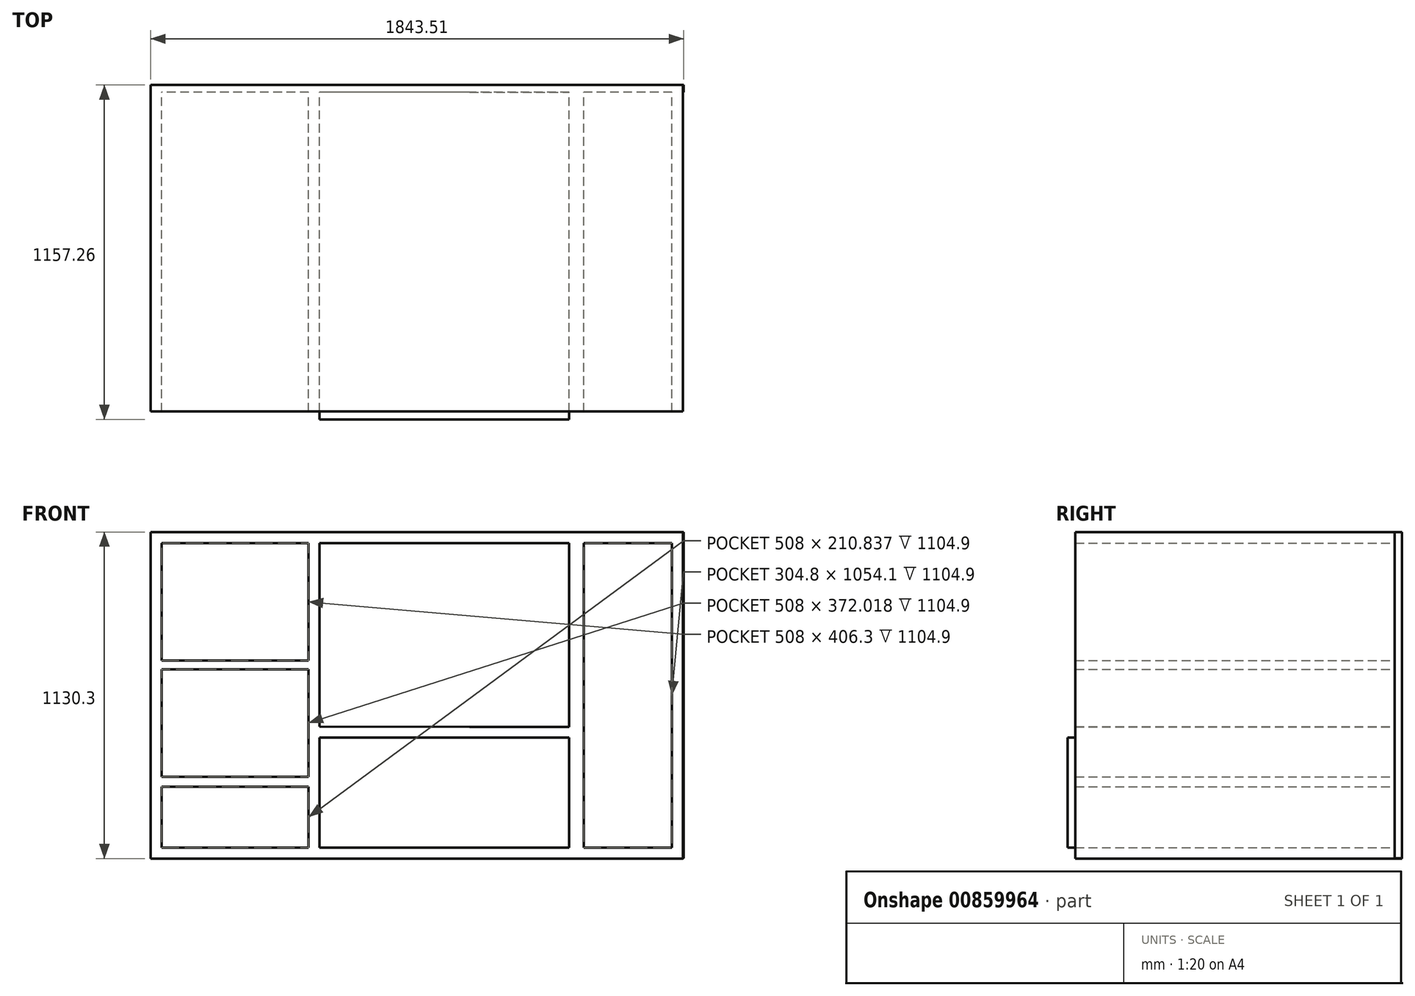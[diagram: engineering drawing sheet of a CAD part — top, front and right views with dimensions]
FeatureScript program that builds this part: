
annotation { "Feature Type Name" : "Feature", "Feature Type Description" : "" }
export const myFeature = defineFeature(function(context is Context, id is Id, definition is map)
    precondition{}
    {
        {
            var Q0;
            Q0=qCreatedBy(makeId("Front.planeOp"),FACE);
            var sketch = newSketch(context, id + "F0", { "sketchPlane" : qUnion([Q0])});
            skLineSegment(sketch, "E0.bottom", {"start": v(920.75, -565.15) * mm, "end": v(-920.75, -565.15) * mm});
            skLineSegment(sketch, "E0.top", {"start": v(920.75, 565.15) * mm, "end": v(-920.75, 565.15) * mm});
            skLineSegment(sketch, "E0.left", {"start": v(920.75, -565.15) * mm, "end": v(920.75, 565.15) * mm});
            skLineSegment(sketch, "E0.right", {"start": v(-920.75, -565.15) * mm, "end": v(-920.75, 565.15) * mm});
            skPoint(sketch, "E0.middle", {"position": v(0, 0) * mm});
            skLineSegment(sketch, "E1.bottom", {"start": v(882.65, -527.05) * mm, "end": v(-882.65, -527.05) * mm});
            skLineSegment(sketch, "E1.top", {"start": v(882.65, 527.05) * mm, "end": v(-882.65, 527.05) * mm});
            skLineSegment(sketch, "E1.left", {"start": v(882.65, -527.05) * mm, "end": v(882.65, 527.05) * mm});
            skLineSegment(sketch, "E2", {"start": v(-336.55, 0) * mm, "end": v(-336.55, -527.05) * mm});
            skLineSegment(sketch, "E3", {"start": v(-336.55, 0) * mm, "end": v(-336.55, 527.05) * mm});
            skPoint(sketch, "E4.start.orphan", {"position": v(-920.75, 0) * mm});
            skLineSegment(sketch, "E5", {"start": v(-882.65, 527.05) * mm, "end": v(-882.65, -527.05) * mm});
            skLineSegment(sketch, "E6", {"start": v(-374.65, -120.67) * mm, "end": v(-374.65, -527.05) * mm});
            skLineSegment(sketch, "E7", {"start": v(-374.65, -120.67) * mm, "end": v(-374.65, 527.05) * mm});
            skLineSegment(sketch, "E8", {"start": v(527.05, -148.89) * mm, "end": v(527.05, -527.05) * mm});
            skLineSegment(sketch, "E9", {"start": v(527.05, -527.05) * mm, "end": v(527.05, -148.89) * mm});
            skLineSegment(sketch, "E10", {"start": v(527.05, -148.89) * mm, "end": v(527.05, 527.05) * mm});
            skLineSegment(sketch, "E11", {"start": v(577.85, -145.72) * mm, "end": v(577.85, -527.05) * mm});
            skLineSegment(sketch, "E12", {"start": v(577.85, -145.72) * mm, "end": v(577.85, 527.05) * mm});
            skPoint(sketch, "E13.orphan", {"position": v(215.3, 0) * mm});
            skPoint(sketch, "E14.end.orphan", {"position": v(-280.78, 0) * mm});
            skLineSegment(sketch, "E15", {"start": v(-336.55, -146.05) * mm, "end": v(527.05, -148.89) * mm});
            skPoint(sketch, "E16.end.orphan", {"position": v(-180.7, -146.05) * mm});
            skLineSegment(sketch, "E17", {"start": v(182.89, -147.76) * mm, "end": v(182.89, -109.66) * mm});
            skLineSegment(sketch, "E18", {"start": v(182.89, -109.66) * mm, "end": v(-336.55, -107.95) * mm});
            skLineSegment(sketch, "E19", {"start": v(182.89, -109.66) * mm, "end": v(527.05, -109.66) * mm});
            skLineSegment(sketch, "E20", {"start": v(-882.65, -316.21) * mm, "end": v(-374.65, -316.21) * mm});
            skPoint(sketch, "E21.end.orphan", {"position": v(-374.65, 203.19) * mm});
            skLineSegment(sketch, "E22", {"start": v(-882.65, 120.75) * mm, "end": v(-374.65, 120.75) * mm});
            skLineSegment(sketch, "E23.bottom", {"start": v(-882.65, 120.75) * mm, "end": v(-752.77, 120.75) * mm});
            skLineSegment(sketch, "E23.top", {"start": v(-882.65, 120.75) * mm, "end": v(-752.77, 120.75) * mm});
            skLineSegment(sketch, "E23.left", {"start": v(-882.65, 120.75) * mm, "end": v(-882.65, 120.75) * mm});
            skLineSegment(sketch, "E23.right", {"start": v(-752.77, 120.75) * mm, "end": v(-752.77, 120.75) * mm});
            skLineSegment(sketch, "E24.bottom", {"start": v(-882.65, 89.88) * mm, "end": v(-408.51, 89.88) * mm});
            skLineSegment(sketch, "E24.top", {"start": v(-882.65, -282.14) * mm, "end": v(-408.51, -282.14) * mm});
            skLineSegment(sketch, "E24.left", {"start": v(-882.65, 89.88) * mm, "end": v(-882.65, -282.14) * mm});
            skLineSegment(sketch, "E25", {"start": v(-408.51, -282.14) * mm, "end": v(-374.65, -282.14) * mm});
            skLineSegment(sketch, "E26", {"start": v(-408.51, 89.88) * mm, "end": v(-374.65, 89.88) * mm});
            skSolve(sketch);
        }
        {
            var Q0;
            Q0=makeQuery(id+"F0.imprint","IMPRINT",FACE,{"disambiguationData":[TD([[makeQuery(id+"F0.imprint","IMPRINT",EDGE,{"derivedFrom":sQuery(id+"F0.wireOp",EDGE,"E0.bottom")}),-1.0]])]});
            var Q1;
            {var subQ4=sQuery(id+"F0.wireOp",EDGE,"E3");Q1=makeQuery(id+"F0.imprint","IMPRINT",FACE,{"disambiguationData":[TD([[makeQuery(id+"F0.imprint","IMPRINT",EDGE,{"derivedFrom":subQ4}),1.0]])]});}
            var Q2;
            {var subQ7=sQuery(id+"F0.wireOp",EDGE,"E24.bottom");Q2=makeQuery(id+"F0.imprint","IMPRINT",FACE,{"disambiguationData":[TD([[makeQuery(id+"F0.imprint","IMPRINT",EDGE,{"derivedFrom":subQ7}),1.0]])]});}
            var Q3;
            {var subQ1=sQuery(id+"F0.wireOp",EDGE,"E20");Q3=makeQuery(id+"F0.imprint","IMPRINT",FACE,{"disambiguationData":[TD([[makeQuery(id+"F0.imprint","IMPRINT",EDGE,{"derivedFrom":subQ1}),1.0]])]});}
            var Q4;
            {var subQ4=sQuery(id+"F0.wireOp",EDGE,"E17");Q4=makeQuery(id+"F0.imprint","IMPRINT",FACE,{"disambiguationData":[TD([[makeQuery(id+"F0.imprint","IMPRINT",EDGE,{"derivedFrom":subQ4}),1.0]])]});}
            var Q5;
            {var subQ4=sQuery(id+"F0.wireOp",EDGE,"E17");Q5=makeQuery(id+"F0.imprint","IMPRINT",FACE,{"disambiguationData":[TD([[makeQuery(id+"F0.imprint","IMPRINT",EDGE,{"derivedFrom":subQ4}),-1.0]])]});}
            var Q6;
            {var subQ4=sQuery(id+"F0.wireOp",EDGE,"E8");Q6=makeQuery(id+"F0.imprint","IMPRINT",FACE,{"disambiguationData":[TD([[makeQuery(id+"F0.imprint","IMPRINT",EDGE,{"derivedFrom":subQ4}),1.0]])]});}
            extrude(context, id + "F1", {"entities" : qUnion([Q0, Q1, Q2, Q3, Q4, Q5, Q6]), "depth" : 1130.3 * mm, "offsetDistance" : 25.4 * mm});
        }
        {
            var Q0;
            Q0=qCreatedBy(makeId("Front.planeOp"),FACE);
            var sketch = newSketch(context, id + "F2", { "sketchPlane" : qUnion([Q0])});
            skLineSegment(sketch, "E27.bottom", {"start": v(-705.9, -446.11) * mm, "end": v(705.9, -446.11) * mm});
            skLineSegment(sketch, "E27.top", {"start": v(-705.9, 446.11) * mm, "end": v(705.9, 446.11) * mm});
            skLineSegment(sketch, "E27.left", {"start": v(-705.9, -446.11) * mm, "end": v(-705.9, 446.11) * mm});
            skLineSegment(sketch, "E27.right", {"start": v(705.9, -446.11) * mm, "end": v(705.9, 446.11) * mm});
            skPoint(sketch, "E27.middle", {"position": v(0, 0) * mm});
            skSolve(sketch);
        }
        {
            var Q0;
            Q0=makeQuery(id+"F2.imprint","IMPRINT",FACE,{"disambiguationData":[TD([[makeQuery(id+"F2.imprint","IMPRINT",EDGE,{"derivedFrom":sQuery(id+"F2.wireOp",EDGE,"E27.bottom")}),1.0]])]});
            var sketch = newSketch(context, id + "F3", { "sketchPlane" : qUnion([Q0])});
            skLineSegment(sketch, "E28.bottom", {"start": v(922.76, 564.64) * mm, "end": v(-904.77, 564.64) * mm});
            skLineSegment(sketch, "E28.top", {"start": v(922.76, -564.93) * mm, "end": v(-904.77, -564.93) * mm});
            skLineSegment(sketch, "E28.left", {"start": v(922.76, 564.64) * mm, "end": v(922.76, -564.93) * mm});
            skLineSegment(sketch, "E28.right", {"start": v(-904.77, 564.64) * mm, "end": v(-904.77, -564.93) * mm});
            skSolve(sketch);
        }
        {
            var Q0;
            Q0 = qSketchRegion(id + "F3", true);
            extrude(context, id + "F4", {"entities" : qUnion([Q0]), "operationType" : NewBodyOperationType.ADD, "depth" : 25.4 * mm, "offsetDistance" : 25.4 * mm});
        }
        {
            var Q0;
            {var subQ1=sQuery(id+"F0.wireOp",EDGE,"E10");Q0=makeQuery(id+"F4.boolean.opBoolean","SPLIT",FACE,{"disambiguationData":[TD([makeQuery(id+"F1.opExtrude","SWEPT_FACE",FACE,{"disambiguationData":[OSD([subQ1])]})])],"derivedFrom":makeQuery(id+"F4.opExtrude","CAP_FACE",FACE,{"disambiguationData":[OSD([sQuery(id+"F3.wireOp",EDGE,"E28.bottom"),sQuery(id+"F3.wireOp",EDGE,"E28.top"),sQuery(id+"F3.wireOp",EDGE,"E28.left"),sQuery(id+"F3.wireOp",EDGE,"E28.right")])],"isStart":false})});}
            var sketch = newSketch(context, id + "F5", { "sketchPlane" : qUnion([Q0])});
            skLineSegment(sketch, "E29.bottom", {"start": v(-337.9, -155.06) * mm, "end": v(527.46, -155.06) * mm});
            skLineSegment(sketch, "E29.top", {"start": v(-337.9, -531.42) * mm, "end": v(527.46, -531.42) * mm});
            skLineSegment(sketch, "E29.left", {"start": v(-337.9, -155.06) * mm, "end": v(-337.9, -531.42) * mm});
            skLineSegment(sketch, "E29.right", {"start": v(527.46, -155.06) * mm, "end": v(527.46, -531.42) * mm});
            skSolve(sketch);
        }
        {
            var Q0;
            Q0 = qSketchRegion(id + "F5", true);
            extrude(context, id + "F6", {"entities" : qUnion([Q0]), "operationType" : NewBodyOperationType.ADD, "oppositeDirection" : true, "depth" : 25.4 * mm, "offsetDistance" : 25.4 * mm});
        }
        {
            var Q0;
            {var subQ1=sQuery(id+"F0.wireOp",EDGE,"E10");Q0=makeQuery(id+"F4.boolean.opBoolean","SPLIT",FACE,{"disambiguationData":[TD([makeQuery(id+"F1.opExtrude","SWEPT_FACE",FACE,{"disambiguationData":[OSD([subQ1])]})])],"derivedFrom":makeQuery(id+"F4.opExtrude","CAP_FACE",FACE,{"disambiguationData":[OSD([sQuery(id+"F3.wireOp",EDGE,"E28.bottom"),sQuery(id+"F3.wireOp",EDGE,"E28.top"),sQuery(id+"F3.wireOp",EDGE,"E28.left"),sQuery(id+"F3.wireOp",EDGE,"E28.right")])],"isStart":false})});}
            var sketch = newSketch(context, id + "F7", { "sketchPlane" : qUnion([Q0])});
            skLineSegment(sketch, "E30.bottom", {"start": v(-281.07, -181.13) * mm, "end": v(550.32, -181.13) * mm});
            skLineSegment(sketch, "E30.top", {"start": v(-281.07, -563.43) * mm, "end": v(550.32, -563.43) * mm});
            skLineSegment(sketch, "E30.left", {"start": v(-281.07, -181.13) * mm, "end": v(-281.07, -563.43) * mm});
            skLineSegment(sketch, "E30.right", {"start": v(550.32, -181.13) * mm, "end": v(550.32, -563.43) * mm});
            skSolve(sketch);
        }
        {
            var Q0;
            Q0 = qSketchRegion(id + "F7", true);
            extrude(context, id + "F8", {"entities" : qUnion([Q0]), "operationType" : NewBodyOperationType.ADD, "oppositeDirection" : true, "depth" : 25.4 * mm, "offsetDistance" : 25.4 * mm});
        }
        {
            var Q0;
            {var subQ2=sQuery(id+"F0.wireOp",EDGE,"E2");Q0=makeQuery(id+"F4.boolean.opBoolean","SPLIT",FACE,{"disambiguationData":[TD([makeQuery(id+"F1.opExtrude","SWEPT_FACE",FACE,{"disambiguationData":[OSD([subQ2])]})])],"derivedFrom":makeQuery(id+"F4.opExtrude","CAP_FACE",FACE,{"disambiguationData":[OSD([sQuery(id+"F3.wireOp",EDGE,"E28.bottom"),sQuery(id+"F3.wireOp",EDGE,"E28.top"),sQuery(id+"F3.wireOp",EDGE,"E28.left"),sQuery(id+"F3.wireOp",EDGE,"E28.right")])],"isStart":false})});}
            var sketch = newSketch(context, id + "F9", { "sketchPlane" : qUnion([Q0])});
            skLineSegment(sketch, "E31.bottom", {"start": v(-336.55, -146.05) * mm, "end": v(527.05, -146.05) * mm});
            skLineSegment(sketch, "E31.top", {"start": v(-336.55, -527.05) * mm, "end": v(527.05, -527.05) * mm});
            skLineSegment(sketch, "E31.left", {"start": v(-336.55, -146.05) * mm, "end": v(-336.55, -527.05) * mm});
            skLineSegment(sketch, "E31.right", {"start": v(527.05, -146.05) * mm, "end": v(527.05, -527.05) * mm});
            skSolve(sketch);
        }
        {
            var Q0;
            Q0 = qSketchRegion(id + "F9", true);
            extrude(context, id + "F10", {"entities" : qUnion([Q0]), "operationType" : NewBodyOperationType.ADD, "depth" : 1131.86 * mm, "offsetDistance" : 25.4 * mm});
        }
        {
            var Q0;
            {var subQ1=sQuery(id+"F0.wireOp",EDGE,"E10");Q0=makeQuery(id+"F4.boolean.opBoolean","SPLIT",FACE,{"disambiguationData":[TD([makeQuery(id+"F1.opExtrude","SWEPT_FACE",FACE,{"disambiguationData":[OSD([subQ1])]})])],"derivedFrom":makeQuery(id+"F4.opExtrude","CAP_FACE",FACE,{"disambiguationData":[OSD([sQuery(id+"F3.wireOp",EDGE,"E28.bottom"),sQuery(id+"F3.wireOp",EDGE,"E28.top"),sQuery(id+"F3.wireOp",EDGE,"E28.left"),sQuery(id+"F3.wireOp",EDGE,"E28.right")])],"isStart":false})});}
            var sketch = newSketch(context, id + "F11", { "sketchPlane" : qUnion([Q0])});
            skLineSegment(sketch, "E32", {"start": v(-650.18, 520.5) * mm, "end": v(-650.18, -521.2) * mm});
            skSolve(sketch);
        }
    });
